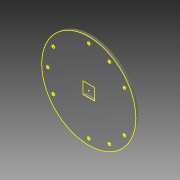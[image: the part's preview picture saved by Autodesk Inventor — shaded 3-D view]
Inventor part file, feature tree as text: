
AUTODESK INVENTOR PART (.ipt)
format: ipt  version: 2015 (Build 190159000, 159)  size: 133,632 bytes
history: native  units: mm
features: sketch x3, extrude x2, projected_geometry x2
ambient origin geometry x8: Origin, YZ Plane, XZ Plane, XY Plane, X Axis, Y Axis, Z Axis, Center Point
bodies: Solid1 (feature_tree)
feature tree (7):
  extrude  "Extrusion1"  Depth=12.8mm
  extrude  "Extrusion2"  Depth=3.0mm TaperAngle=0.0deg
  sketch  "Sketch3"  dims[d5=120.0deg d6=120.0deg d7=90.0mm d8=30.0deg d9=30.0deg d10=30.0deg d11=30.0deg d12=30.0deg d13=30.0deg d14=30.0deg d15=30.0deg d16=3.0mm d17=3.0mm d18=3.0mm d19=3.0mm d20=3.0mm d21=3.0mm d22=3.0mm d23=3.0mm d24=3.0mm d25=3.0mm d26=0.0mm]
  sketch  "Sketch1"  dims[d0=103.0mm d1=12.8mm]
  sketch  "Sketch2"  dims[d2=12.8mm d3=3.0mm d4=0.0mm]
  projected_geometry  "Projected Loop1"
  projected_geometry  "Projected Loop2"
